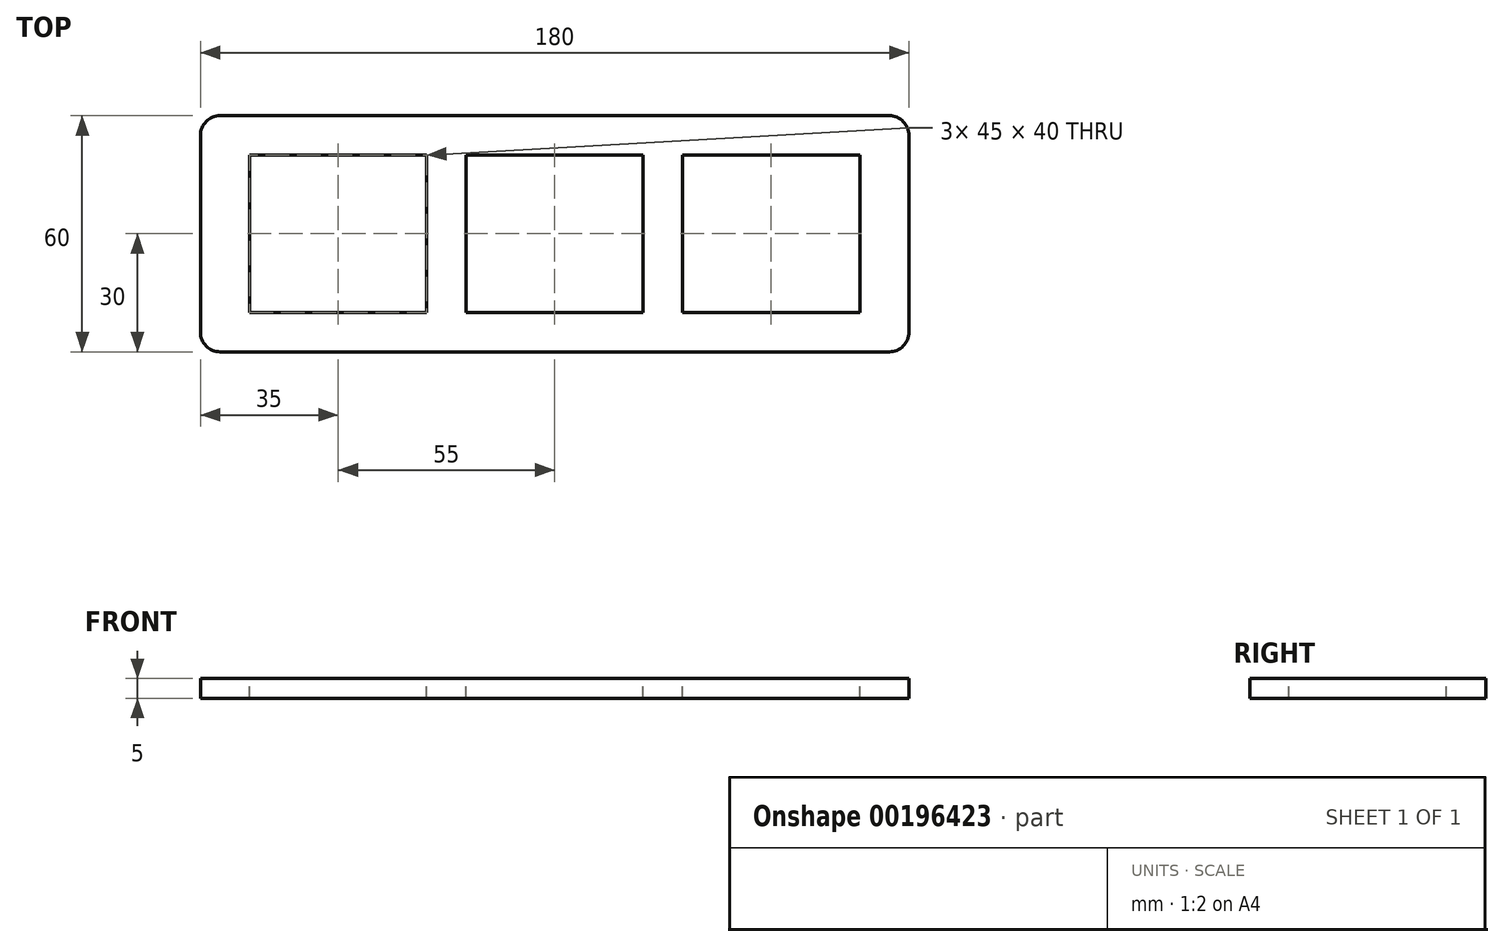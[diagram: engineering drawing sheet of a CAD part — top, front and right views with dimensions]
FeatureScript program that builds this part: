
annotation { "Feature Type Name" : "Feature", "Feature Type Description" : "" }
export const myFeature = defineFeature(function(context is Context, id is Id, definition is map)
    precondition{}
    {
        {
            var Q0;
            Q0=qCreatedBy(makeId("Top.planeOp"),FACE);
            var sketch = newSketch(context, id + "F0", { "sketchPlane" : qUnion([Q0])});
            skLineSegment(sketch, "E0.bottom", {"start": v(85, -30) * mm, "end": v(-85, -30) * mm});
            skLineSegment(sketch, "E0.top", {"start": v(85, 30) * mm, "end": v(-85, 30) * mm});
            skLineSegment(sketch, "E0.left", {"start": v(90, -25) * mm, "end": v(90, 25) * mm});
            skLineSegment(sketch, "E0.right", {"start": v(-90, -25) * mm, "end": v(-90, 25) * mm});
            skPoint(sketch, "E0.middle", {"position": v(0, 0) * mm});
            skPoint(sketch, "E1.visualSharp", {"position": v(-90, 30) * mm});
            skArc(sketch, "E1.filletArc", {"start": v(-85, 30) * mm, "mid": v(-88.54, 28.54) * mm, "end": v(-90, 25) * mm});
            skPoint(sketch, "E2.visualSharp", {"position": v(-90, -30) * mm});
            skArc(sketch, "E2.filletArc", {"start": v(-90, -25) * mm, "mid": v(-88.54, -28.54) * mm, "end": v(-85, -30) * mm});
            skPoint(sketch, "E3.visualSharp", {"position": v(90, -30) * mm});
            skArc(sketch, "E3.filletArc", {"start": v(85, -30) * mm, "mid": v(88.54, -28.54) * mm, "end": v(90, -25) * mm});
            skPoint(sketch, "E4.visualSharp", {"position": v(90, 30) * mm});
            skArc(sketch, "E4.filletArc", {"start": v(90, 25) * mm, "mid": v(88.54, 28.54) * mm, "end": v(85, 30) * mm});
            skSolve(sketch);
        }
        {
            var Q0;
            Q0 = qSketchRegion(id + "F0", true);
            extrude(context, id + "F1", {"entities" : qUnion([Q0]), "depth" : 5 * mm});
        }
        {
            var Q0;
            Q0=makeQuery(id+"F1.opExtrude","CAP_FACE",FACE,{"disambiguationData":[OSD([sQuery(id+"F0.wireOp",EDGE,"E0.bottom"),sQuery(id+"F0.wireOp",EDGE,"E0.top"),sQuery(id+"F0.wireOp",EDGE,"E0.left"),sQuery(id+"F0.wireOp",EDGE,"E0.right")])],"isStart":false});
            var sketch = newSketch(context, id + "F2", { "sketchPlane" : qUnion([Q0])});
            skLineSegment(sketch, "E5", {"start": v(-90, 0) * mm, "end": v(90, 0) * mm, "construction": true});
            skLineSegment(sketch, "E6.bottom", {"start": v(22.5, -20) * mm, "end": v(-22.5, -20) * mm});
            skLineSegment(sketch, "E6.top", {"start": v(22.5, 20) * mm, "end": v(-22.5, 20) * mm});
            skLineSegment(sketch, "E6.left", {"start": v(22.5, -20) * mm, "end": v(22.5, 20) * mm});
            skLineSegment(sketch, "E6.right", {"start": v(-22.5, -20) * mm, "end": v(-22.5, 20) * mm});
            skPoint(sketch, "E6.middle", {"position": v(0, 0) * mm});
            skLineSegment(sketch, "E7.bottom", {"start": v(77.5, -20) * mm, "end": v(32.5, -20) * mm});
            skLineSegment(sketch, "E7.top", {"start": v(77.5, 20) * mm, "end": v(32.5, 20) * mm});
            skLineSegment(sketch, "E7.left", {"start": v(77.5, -20) * mm, "end": v(77.5, 20) * mm});
            skLineSegment(sketch, "E7.right", {"start": v(32.5, -20) * mm, "end": v(32.5, 20) * mm});
            skPoint(sketch, "E7.middle", {"position": v(55, 0) * mm});
            skLineSegment(sketch, "E8.bottom", {"start": v(-32.5, 20) * mm, "end": v(-77.5, 20) * mm});
            skLineSegment(sketch, "E8.top", {"start": v(-32.5, -20) * mm, "end": v(-77.5, -20) * mm});
            skLineSegment(sketch, "E8.left", {"start": v(-32.5, 20) * mm, "end": v(-32.5, -20) * mm});
            skLineSegment(sketch, "E8.right", {"start": v(-77.5, 20) * mm, "end": v(-77.5, -20) * mm});
            skPoint(sketch, "E8.middle", {"position": v(-55, 0) * mm});
            skLineSegment(sketch, "E9", {"start": v(-32.5, 20) * mm, "end": v(-22.5, 20) * mm, "construction": true});
            skLineSegment(sketch, "E10", {"start": v(22.5, 20) * mm, "end": v(32.5, 20) * mm, "construction": true});
            skSolve(sketch);
        }
        {
            var Q0;
            Q0 = qSketchRegion(id + "F2", true);
            extrude(context, id + "F3", {"entities" : qUnion([Q0]), "operationType" : NewBodyOperationType.REMOVE, "oppositeDirection" : true, "depth" : 5 * mm});
        }
    });
